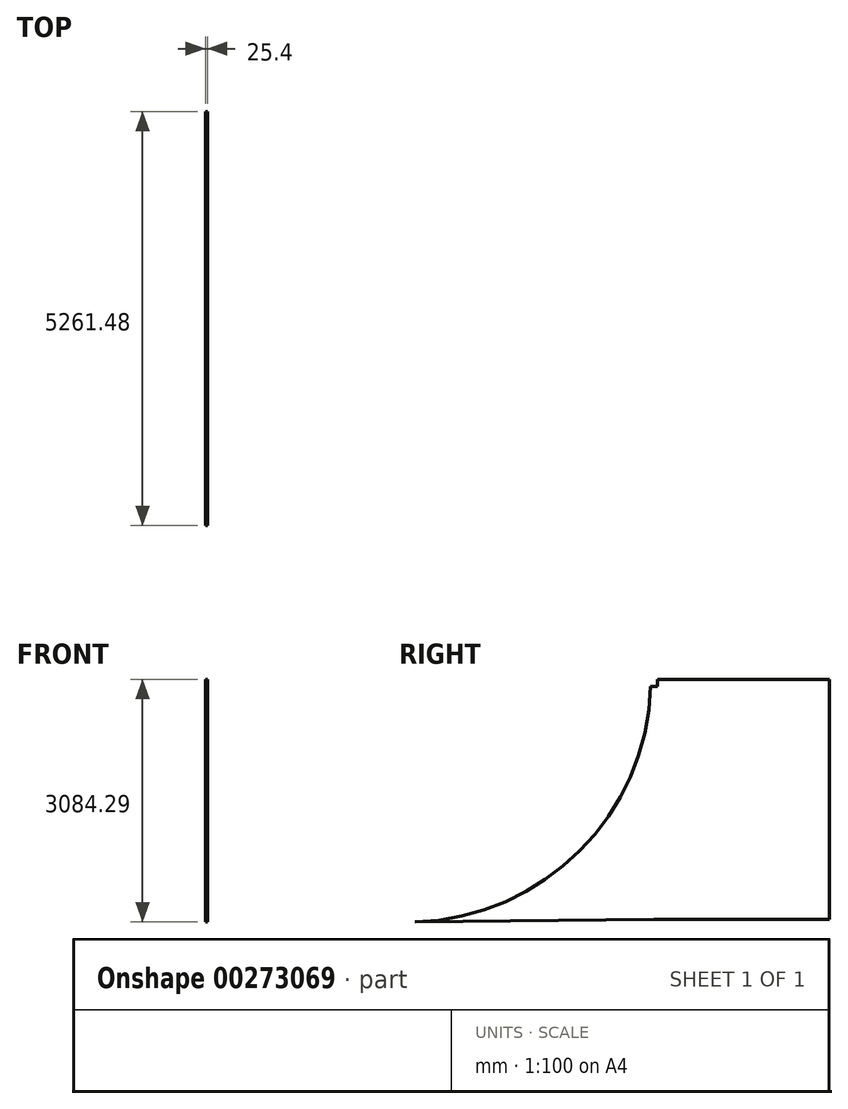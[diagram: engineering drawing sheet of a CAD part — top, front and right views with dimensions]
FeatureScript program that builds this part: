
annotation { "Feature Type Name" : "Feature", "Feature Type Description" : "" }
export const myFeature = defineFeature(function(context is Context, id is Id, definition is map)
    precondition{}
    {
        {
            var Q0;
            Q0=qCreatedBy(makeId("Right.planeOp"),FACE);
            var sketch = newSketch(context, id + "F0", { "sketchPlane" : qUnion([Q0])});
            skLineSegment(sketch, "E0.bottom", {"start": v(455.7, 1529.44) * mm, "end": v(2635.5, 1529.44) * mm});
            skLineSegment(sketch, "E0.top", {"start": v(409.98, -1518.56) * mm, "end": v(2635.5, -1518.56) * mm});
            skLineSegment(sketch, "E0.right", {"start": v(2635.5, 1529.44) * mm, "end": v(2635.5, -1518.56) * mm});
            skArc(sketch, "E1", {"start": v(-2625.98, -1554.85) * mm, "mid": v(-534.47, -651.75) * mm, "end": v(366.8, 1440.54) * mm});
            skLineSegment(sketch, "E2", {"start": v(-2625.98, -1554.85) * mm, "end": v(409.98, -1518.56) * mm});
            skLineSegment(sketch, "E3.bottom", {"start": v(366.8, 1440.54) * mm, "end": v(455.7, 1440.54) * mm});
            skLineSegment(sketch, "E3.right", {"start": v(455.7, 1440.54) * mm, "end": v(455.7, 1529.44) * mm});
            skSolve(sketch);
        }
        {
            var Q0;
            Q0 = qSketchRegion(id + "F0", true);
            extrude(context, id + "F1", {"entities" : qUnion([Q0]), "depth" : 25.4 * mm});
        }
    });
